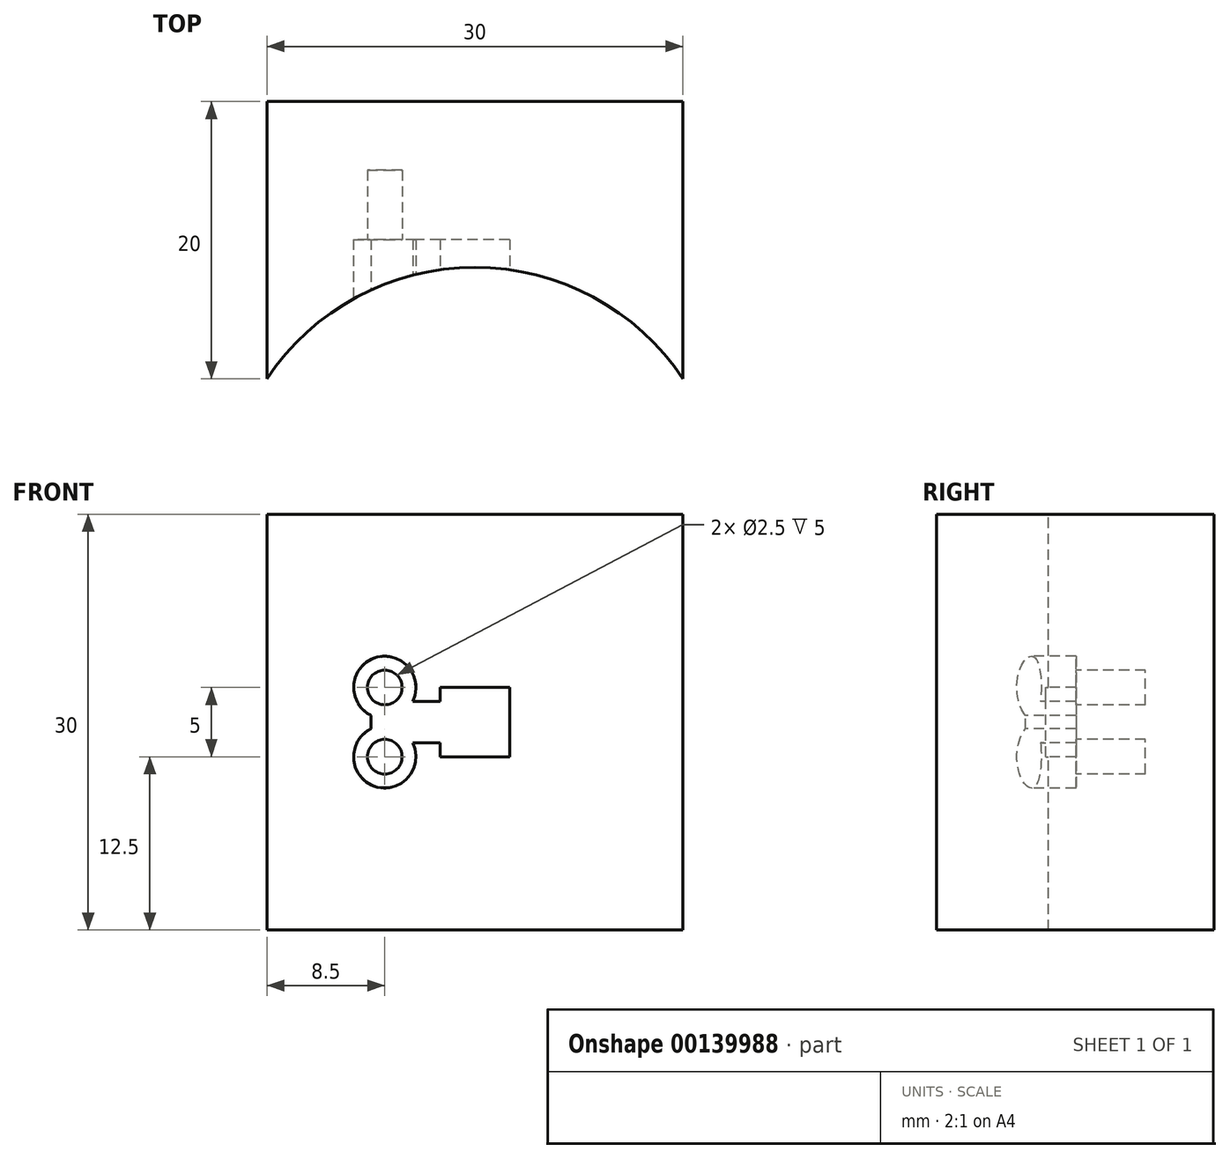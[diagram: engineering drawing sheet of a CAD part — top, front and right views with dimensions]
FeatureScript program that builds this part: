
annotation { "Feature Type Name" : "Feature", "Feature Type Description" : "" }
export const myFeature = defineFeature(function(context is Context, id is Id, definition is map)
    precondition{}
    {
        {
            var Q0;
            Q0=qCreatedBy(makeId("Front.planeOp"),FACE);
            var sketch = newSketch(context, id + "F0", { "sketchPlane" : qUnion([Q0])});
            skLineSegment(sketch, "E0.bottom", {"start": v(0, 0) * mm, "end": v(30, 0) * mm});
            skLineSegment(sketch, "E0.top", {"start": v(0, 30) * mm, "end": v(30, 30) * mm});
            skLineSegment(sketch, "E0.left", {"start": v(0, 0) * mm, "end": v(0, 30) * mm});
            skLineSegment(sketch, "E0.right", {"start": v(30, 0) * mm, "end": v(30, 30) * mm});
            skSolve(sketch);
        }
        {
            var Q0;
            Q0 = qSketchRegion(id + "F0", true);
            extrude(context, id + "F1", {"entities" : qUnion([Q0]), "depth" : 20 * mm});
        }
        {
            var Q0;
            Q0=makeQuery(id+"F1.opExtrude","SWEPT_FACE",FACE,{"disambiguationData":[OSD([sQuery(id+"F0.wireOp",EDGE,"E0.top")])]});
            var sketch = newSketch(context, id + "F2", { "sketchPlane" : qUnion([Q0])});
            skArc(sketch, "E1", {"start": v(30, -20) * mm, "mid": v(15, -11.95) * mm, "end": v(0, -20) * mm});
            skLineSegment(sketch, "E2", {"start": v(0, -20) * mm, "end": v(30, -20) * mm});
            skPoint(sketch, "E3", {"position": v(15, -11.95) * mm});
            skSolve(sketch);
        }
        {
            var Q0;
            Q0 = qSketchRegion(id + "F2", true);
            extrude(context, id + "F3", {"entities" : qUnion([Q0]), "operationType" : NewBodyOperationType.REMOVE, "endBound" : BoundingType.THROUGH_ALL, "oppositeDirection" : true, "depth" : 25 * mm});
        }
        {
            var Q0;
            Q0=makeQuery(id+"F1.opExtrude","SWEPT_FACE",FACE,{"disambiguationData":[OSD([sQuery(id+"F0.wireOp",EDGE,"E0.top")])]});
            var sketch = newSketch(context, id + "F4", { "sketchPlane" : qUnion([Q0])});
            skPoint(sketch, "E4", {"position": v(15, -11.95) * mm});
            skSolve(sketch);
        }
        {
            var Q0;
            Q0=qCreatedBy(makeId("Front.planeOp"),FACE);
            var Q1;
            Q1=sQuery(id+"F4.wireOp",VERTEX,"E4");
            cPlane(context, id + "F5", {"entities" : qUnion([Q0, Q1]), "cplaneType" : CPlaneType.PLANE_POINT, "offset" : 25 * mm, "width" : 150 * mm, "height" : 150 * mm});
        }
        {
            var Q0;
            Q0=qCreatedBy(id+"F5.planeOp",FACE);
            cPlane(context, id + "F6", {"entities" : qUnion([Q0]), "cplaneType" : CPlaneType.OFFSET, "offset" : 1 * mm, "width" : 150 * mm, "height" : 150 * mm});
        }
        {
            var Q0;
            Q0=qCreatedBy(id+"F6.planeOp",FACE);
            var sketch = newSketch(context, id + "F7", { "sketchPlane" : qUnion([Q0])});
            skLineSegment(sketch, "E5.0.0", {"start": v(30, 0) * mm, "end": v(30, 30) * mm, "construction": true});
            skLineSegment(sketch, "E5.0.1", {"start": v(30, 30) * mm, "end": v(0, 30) * mm, "construction": true});
            skLineSegment(sketch, "E5.0.2", {"start": v(0, 30) * mm, "end": v(0, 0) * mm, "construction": true});
            skLineSegment(sketch, "E5.0.3", {"start": v(0, 0) * mm, "end": v(30, 0) * mm, "construction": true});
            skLineSegment(sketch, "E6", {"start": v(15, 30) * mm, "end": v(15, 0) * mm, "construction": true});
            skLineSegment(sketch, "E7", {"start": v(0, 15) * mm, "end": v(30, 15) * mm, "construction": true});
            skLineSegment(sketch, "E8", {"start": v(15, 17.5) * mm, "end": v(17.5, 17.5) * mm});
            skLineSegment(sketch, "E9", {"start": v(17.5, 17.5) * mm, "end": v(17.5, 15) * mm});
            skLineSegment(sketch, "E10", {"start": v(17.5, 15) * mm, "end": v(17.5, 12.5) * mm});
            skLineSegment(sketch, "E11", {"start": v(17.5, 12.5) * mm, "end": v(12.5, 12.5) * mm});
            skLineSegment(sketch, "E12", {"start": v(12.5, 12.5) * mm, "end": v(12.5, 17.5) * mm});
            skLineSegment(sketch, "E13", {"start": v(12.5, 17.5) * mm, "end": v(15, 17.5) * mm});
            skLineSegment(sketch, "E14", {"start": v(12.5, 16.5) * mm, "end": v(7.5, 16.5) * mm});
            skLineSegment(sketch, "E15", {"start": v(7.5, 16.5) * mm, "end": v(7.5, 15) * mm});
            skLineSegment(sketch, "E16", {"start": v(7.5, 15) * mm, "end": v(7.5, 13.5) * mm});
            skLineSegment(sketch, "E17", {"start": v(7.5, 13.5) * mm, "end": v(12.5, 13.5) * mm});
            skSolve(sketch);
        }
        {
            var Q0;
            Q0 = qSketchRegion(id + "F7", true);
            extrude(context, id + "F8", {"entities" : qUnion([Q0]), "operationType" : NewBodyOperationType.REMOVE, "oppositeDirection" : true, "depth" : 3 * mm});
        }
        {
            var Q0;
            Q0 = qSketchRegion(id + "F7", true);
            extrude(context, id + "F9", {"entities" : qUnion([Q0]), "operationType" : NewBodyOperationType.REMOVE, "endBound" : BoundingType.THROUGH_ALL, "depth" : 25 * mm});
        }
        {
            var Q0;
            Q0=qCreatedBy(id+"F6.planeOp",FACE);
            var sketch = newSketch(context, id + "F10", { "sketchPlane" : qUnion([Q0])});
            skLineSegment(sketch, "E18.0.0", {"start": v(30, 0) * mm, "end": v(30, 30) * mm, "construction": true});
            skLineSegment(sketch, "E18.0.1", {"start": v(30, 30) * mm, "end": v(0, 30) * mm, "construction": true});
            skLineSegment(sketch, "E18.0.2", {"start": v(0, 30) * mm, "end": v(0, 0) * mm, "construction": true});
            skLineSegment(sketch, "E18.0.3", {"start": v(0, 0) * mm, "end": v(30, 0) * mm, "construction": true});
            skLineSegment(sketch, "E19", {"start": v(0, 15) * mm, "end": v(30, 15) * mm, "construction": true});
            skLineSegment(sketch, "E20.0", {"start": v(12.5, 17.5) * mm, "end": v(12.5, 16.5) * mm, "construction": true});
            skLineSegment(sketch, "E21.0", {"start": v(12.5, 13.5) * mm, "end": v(12.5, 12.5) * mm, "construction": true});
            skCircle(sketch, "E22", {"center": v(8.5, 17.5) * mm, "radius": 1.25 * mm});
            skCircle(sketch, "E23", {"center": v(8.5, 12.5) * mm, "radius": 1.25 * mm});
            skLineSegment(sketch, "E24", {"start": v(8.5, 12.5) * mm, "end": v(8.5, 15) * mm, "construction": true});
            skLineSegment(sketch, "E25", {"start": v(8.5, 17.5) * mm, "end": v(8.5, 15) * mm, "construction": true});
            skSolve(sketch);
        }
        {
            var Q0;
            Q0 = qSketchRegion(id + "F10", true);
            extrude(context, id + "F11", {"entities" : qUnion([Q0]), "operationType" : NewBodyOperationType.REMOVE, "oppositeDirection" : true, "depth" : 8 * mm});
        }
        {
            var Q0;
            Q0 = qSketchRegion(id + "F10", true);
            extrude(context, id + "F12", {"entities" : qUnion([Q0]), "operationType" : NewBodyOperationType.REMOVE, "endBound" : BoundingType.THROUGH_ALL, "depth" : 25 * mm});
        }
        {
            var Q0;
            Q0=makeQuery(id+"F8.boolean.opBoolean","COPY",FACE,{"derivedFrom":makeQuery(id+"F8.opExtrude","CAP_FACE",FACE,{"disambiguationData":[OSD([sQuery(id+"F7.wireOp",EDGE,"E8"),sQuery(id+"F7.wireOp",EDGE,"E9"),sQuery(id+"F7.wireOp",EDGE,"E10"),sQuery(id+"F7.wireOp",EDGE,"E11"),sQuery(id+"F7.wireOp",EDGE,"E12"),sQuery(id+"F7.wireOp",EDGE,"E13"),sQuery(id+"F7.wireOp",EDGE,"E14"),sQuery(id+"F7.wireOp",EDGE,"E15"),sQuery(id+"F7.wireOp",EDGE,"E16"),sQuery(id+"F7.wireOp",EDGE,"E17")])],"isStart":false})});
            var Q1;
            {var subQ0=sQuery(id+"F7.wireOp",EDGE,"E14");Q1=makeQuery(id+"F11.boolean.opBoolean","INTERSECT",VERTEX,{"derivedFrom":[makeQuery(id+"F9.boolean.opBoolean","MERGE",FACE,{"derivedFrom":[makeQuery(id+"F8.boolean.opBoolean","COPY",FACE,{"derivedFrom":makeQuery(id+"F8.opExtrude","SWEPT_FACE",FACE,{"disambiguationData":[OSD([subQ0])]})}),makeQuery(id+"F9.opExtrude","SWEPT_FACE",FACE,{"disambiguationData":[OSD([subQ0])]})]}),makeQuery(id+"F3.boolean.opBoolean","COPY",FACE,{"derivedFrom":makeQuery(id+"F3.opExtrude","SWEPT_FACE",FACE,{"disambiguationData":[OSD([sQuery(id+"F2.wireOp",EDGE,"E1")])]})}),makeQuery(id+"F11.opExtrude","SWEPT_FACE",FACE,{"disambiguationData":[OSD([sQuery(id+"F10.wireOp",EDGE,"E22")])]})]});}
            cPlane(context, id + "F13", {"entities" : qUnion([Q0, Q1]), "cplaneType" : CPlaneType.PLANE_POINT, "offset" : 25 * mm, "width" : 150 * mm, "height" : 150 * mm});
        }
        {
            var Q0;
            Q0=qCreatedBy(id+"F13.planeOp",FACE);
            var sketch = newSketch(context, id + "F14", { "sketchPlane" : qUnion([Q0])});
            skArc(sketch, "E26.0", {"start": v(7.75, 16.5) * mm, "mid": v(8.5, 18.75) * mm, "end": v(9.25, 16.5) * mm, "construction": true});
            skArc(sketch, "E27.0", {"start": v(9.25, 13.5) * mm, "mid": v(8.5, 11.25) * mm, "end": v(7.75, 13.5) * mm, "construction": true});
            skCircle(sketch, "E28", {"center": v(8.5, 17.5) * mm, "radius": 2.25 * mm});
            skCircle(sketch, "E29", {"center": v(8.5, 12.5) * mm, "radius": 2.25 * mm});
            skSolve(sketch);
        }
        {
            var Q0;
            Q0 = qSketchRegion(id + "F14", true);
            var Q1;
            Q1=makeQuery(id+"F8.boolean.opBoolean","COPY",FACE,{"derivedFrom":makeQuery(id+"F8.opExtrude","CAP_FACE",FACE,{"disambiguationData":[OSD([sQuery(id+"F7.wireOp",EDGE,"E8"),sQuery(id+"F7.wireOp",EDGE,"E9"),sQuery(id+"F7.wireOp",EDGE,"E10"),sQuery(id+"F7.wireOp",EDGE,"E11"),sQuery(id+"F7.wireOp",EDGE,"E12"),sQuery(id+"F7.wireOp",EDGE,"E13"),sQuery(id+"F7.wireOp",EDGE,"E14"),sQuery(id+"F7.wireOp",EDGE,"E15"),sQuery(id+"F7.wireOp",EDGE,"E16"),sQuery(id+"F7.wireOp",EDGE,"E17")])],"isStart":false})});
            extrude(context, id + "F15", {"entities" : qUnion([Q0]), "operationType" : NewBodyOperationType.REMOVE, "endBound" : BoundingType.UP_TO_SURFACE, "oppositeDirection" : true, "endBoundEntityFace" : qUnion([Q1]), "depth" : 25 * mm});
        }
        {
            var Q0;
            Q0 = qSketchRegion(id + "F14", true);
            extrude(context, id + "F16", {"entities" : qUnion([Q0]), "operationType" : NewBodyOperationType.REMOVE, "endBound" : BoundingType.THROUGH_ALL, "depth" : 25 * mm});
        }
    });
